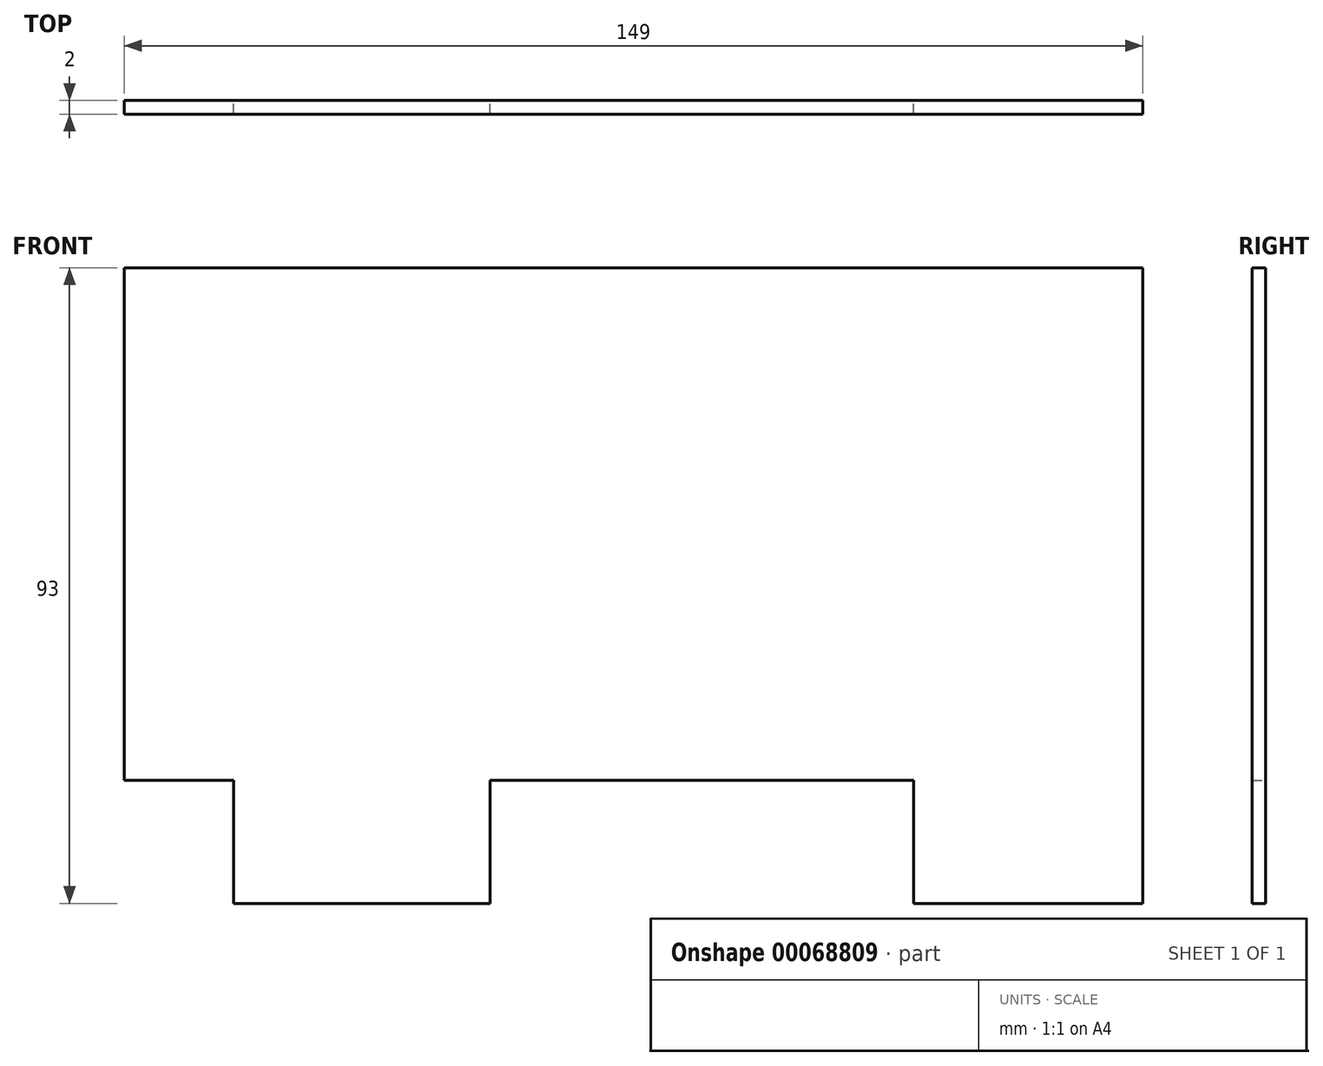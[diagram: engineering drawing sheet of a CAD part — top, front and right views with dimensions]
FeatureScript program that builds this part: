
annotation { "Feature Type Name" : "Feature", "Feature Type Description" : "" }
export const myFeature = defineFeature(function(context is Context, id is Id, definition is map)
    precondition{}
    {
        {
            var Q0;
            Q0=qCreatedBy(makeId("Front.planeOp"),FACE);
            var sketch = newSketch(context, id + "F0", { "sketchPlane" : qUnion([Q0])});
            skLineSegment(sketch, "E0", {"start": v(0, 0) * mm, "end": v(0, 93) * mm});
            skLineSegment(sketch, "E1", {"start": v(0, 93) * mm, "end": v(-149, 93) * mm});
            skLineSegment(sketch, "E2", {"start": v(-33.5, 0) * mm, "end": v(-33.5, 18) * mm});
            skLineSegment(sketch, "E3", {"start": v(-33.5, 18) * mm, "end": v(-95.5, 18) * mm});
            skLineSegment(sketch, "E4", {"start": v(-95.5, 18) * mm, "end": v(-95.5, 0) * mm});
            skLineSegment(sketch, "E5", {"start": v(0, 0) * mm, "end": v(-33.5, 0) * mm});
            skLineSegment(sketch, "E6", {"start": v(-133, 0) * mm, "end": v(-133, 18) * mm});
            skLineSegment(sketch, "E7", {"start": v(-133, 18) * mm, "end": v(-149, 18) * mm});
            skLineSegment(sketch, "E8", {"start": v(-149, 93) * mm, "end": v(-149, 18) * mm});
            skLineSegment(sketch, "E9", {"start": v(-133, 0) * mm, "end": v(-95.5, 0) * mm});
            skSolve(sketch);
        }
        {
            var Q0;
            Q0 = qSketchRegion(id + "F0", true);
            extrude(context, id + "F1", {"entities" : qUnion([Q0]), "depth" : 2 * mm});
        }
    });
